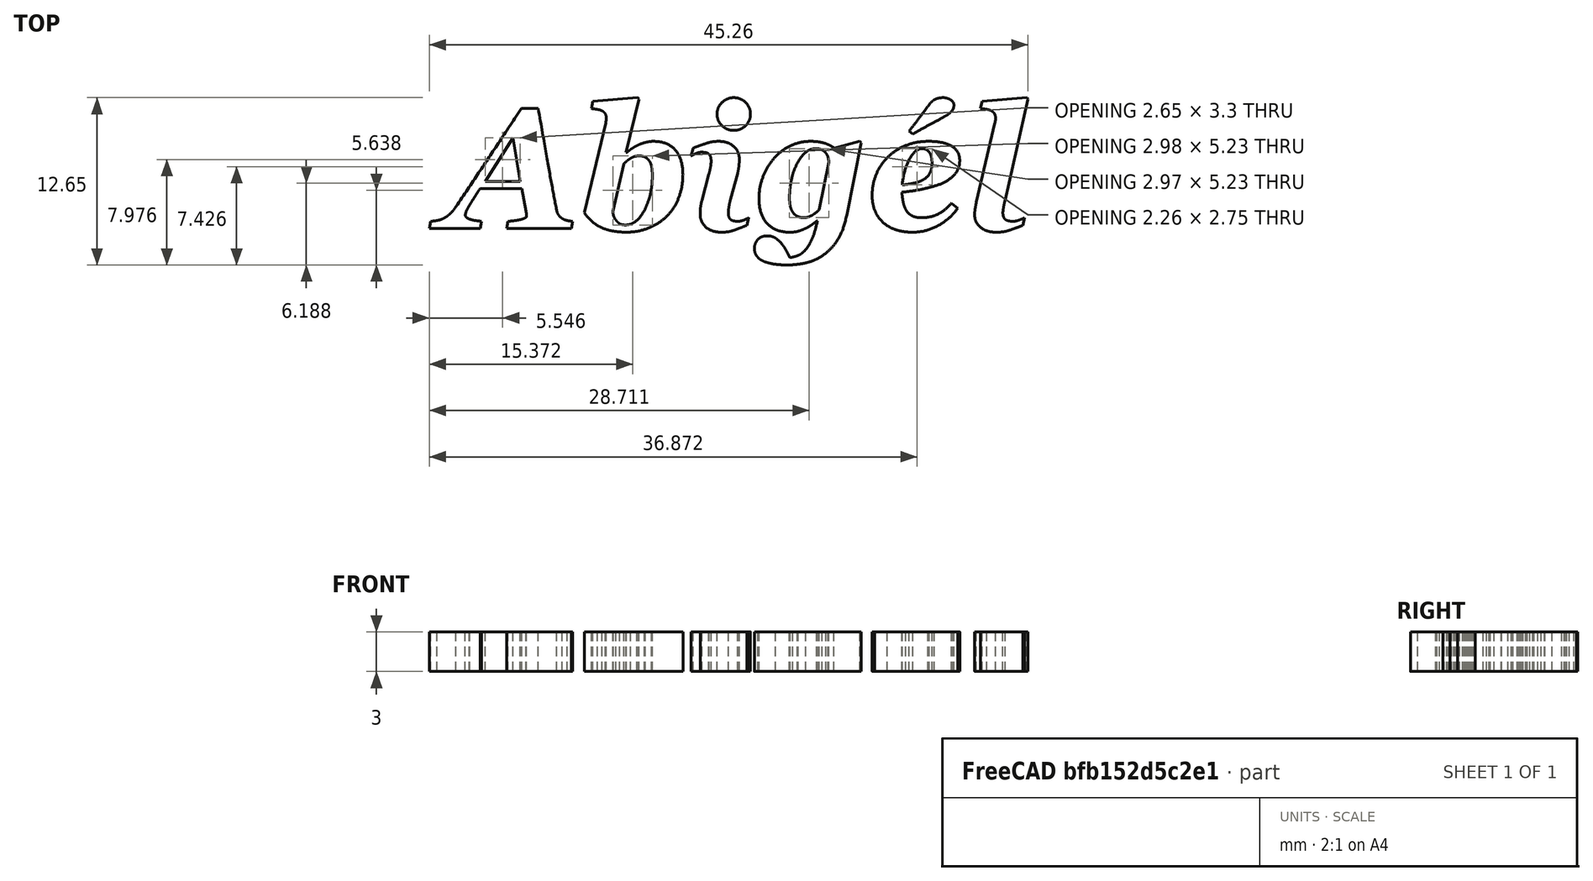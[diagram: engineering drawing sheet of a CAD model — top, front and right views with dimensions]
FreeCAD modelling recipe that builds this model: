
FCSTD DOCUMENT  (FreeCAD 0.17R13541 (Git))
Label: Aby
License: All rights reserved
LicenseURL: http://en.wikipedia.org/wiki/All_rights_reserved
objects: Sketcher::SketchObject×1, Part::Extrusion×1
note: 2 computed .brp shape members not serialized (recipe doc carries the construction recipe); baked Part::Feature solids carry a one-line shape summary decoded from their .brp

FEATURE [Sketcher::SketchObject] Sketch
  sketch-geometry (226):
    g0: LineSegment StartX=4.71852 StartY=0 StartZ=0 EndX=4.83025 EndY=0.550064 EndZ=0
    g1: LineSegment StartX=9.61324 StartY=0 StartZ=0 EndX=4.71852 EndY=0 EndZ=0
    g2: LineSegment StartX=9.72067 StartY=0.550064 StartZ=0 EndX=9.61324 EndY=0 EndZ=0
    g3: BSplineCurve PolesCount=3 KnotsCount=2 Degree=2 IsPeriodic=0
    g4: BSplineCurve PolesCount=3 KnotsCount=2 Degree=2 IsPeriodic=0
    g5: BSplineCurve PolesCount=3 KnotsCount=2 Degree=2 IsPeriodic=0
    g6: BSplineCurve PolesCount=3 KnotsCount=2 Degree=2 IsPeriodic=0
    g7: BSplineCurve PolesCount=3 KnotsCount=2 Degree=2 IsPeriodic=0
    g8: BSplineCurve PolesCount=3 KnotsCount=2 Degree=2 IsPeriodic=0
    g9: LineSegment StartX=5.83584 StartY=9.07606 StartZ=0 EndX=7.11216 EndY=9.07606 EndZ=0
    g10: BSplineCurve PolesCount=3 KnotsCount=2 Degree=2 IsPeriodic=0
    g11: BSplineCurve PolesCount=3 KnotsCount=2 Degree=2 IsPeriodic=0
    g12: BSplineCurve PolesCount=3 KnotsCount=2 Degree=2 IsPeriodic=0
    g13: BSplineCurve PolesCount=3 KnotsCount=2 Degree=2 IsPeriodic=0
    g14: BSplineCurve PolesCount=3 KnotsCount=2 Degree=2 IsPeriodic=0
    g15: BSplineCurve PolesCount=3 KnotsCount=2 Degree=2 IsPeriodic=0
    g16: LineSegment StartX=-1.12162 StartY=0 StartZ=0 EndX=-1.00988 EndY=0.550064 EndZ=0
    g17: LineSegment StartX=2.72024 StartY=0 StartZ=0 EndX=-1.12162 EndY=0 EndZ=0
    g18: LineSegment StartX=2.83197 StartY=0.550064 StartZ=0 EndX=2.72024 EndY=0 EndZ=0
    g19: BSplineCurve PolesCount=3 KnotsCount=2 Degree=2 IsPeriodic=0
    g20: BSplineCurve PolesCount=3 KnotsCount=2 Degree=2 IsPeriodic=0
    g21: BSplineCurve PolesCount=3 KnotsCount=2 Degree=2 IsPeriodic=0
    g22: BSplineCurve PolesCount=3 KnotsCount=2 Degree=2 IsPeriodic=0
    g23: BSplineCurve PolesCount=3 KnotsCount=2 Degree=2 IsPeriodic=0
    g24: BSplineCurve PolesCount=3 KnotsCount=2 Degree=2 IsPeriodic=0
    g25: LineSegment StartX=5.86592 StartY=3.02535 StartZ=0 EndX=2.71594 EndY=3.02535 EndZ=0
    g26: LineSegment StartX=6.18823 StartY=1.315 StartZ=0 EndX=5.86592 EndY=3.02535 EndZ=0
    g27: BSplineCurve PolesCount=3 KnotsCount=2 Degree=2 IsPeriodic=0
    g28: BSplineCurve PolesCount=3 KnotsCount=2 Degree=2 IsPeriodic=0
    g29: BSplineCurve PolesCount=3 KnotsCount=2 Degree=2 IsPeriodic=0
    g30: BSplineCurve PolesCount=3 KnotsCount=2 Degree=2 IsPeriodic=0
    g31: LineSegment StartX=5.74989 StartY=3.57542 StartZ=0 EndX=5.19123 EndY=6.87581 EndZ=0
    g32: LineSegment StartX=3.10271 StartY=3.57542 StartZ=0 EndX=5.74989 EndY=3.57542 EndZ=0
    g33: LineSegment StartX=5.19123 StartY=6.87581 StartZ=0 EndX=3.10271 EndY=3.57542 EndZ=0
    g34: BSplineCurve PolesCount=3 KnotsCount=2 Degree=2 IsPeriodic=0
    g35: BSplineCurve PolesCount=3 KnotsCount=2 Degree=2 IsPeriodic=0
    g36: BSplineCurve PolesCount=3 KnotsCount=2 Degree=2 IsPeriodic=0
    g37: BSplineCurve PolesCount=3 KnotsCount=2 Degree=2 IsPeriodic=0
    g38: BSplineCurve PolesCount=3 KnotsCount=2 Degree=2 IsPeriodic=0
    g39: BSplineCurve PolesCount=3 KnotsCount=2 Degree=2 IsPeriodic=0
    g40: BSplineCurve PolesCount=3 KnotsCount=2 Degree=2 IsPeriodic=0
    g41: LineSegment StartX=13.743 StartY=5.7413 StartZ=0 EndX=13.7903 EndY=5.7413 EndZ=0
    g42: LineSegment StartX=14.7185 StartY=9.80232 StartZ=0 EndX=13.743 EndY=5.7413 EndZ=0
    g43: LineSegment StartX=14.6498 StartY=9.90116 StartZ=0 EndX=14.7185 EndY=9.80232 EndZ=0
    g44: LineSegment StartX=11.2505 StartY=9.62613 StartZ=0 EndX=14.6498 EndY=9.90116 EndZ=0
    g45: LineSegment StartX=11.1345 StartY=9.07606 StartZ=0 EndX=11.2505 EndY=9.62613 EndZ=0
    g46: BSplineCurve PolesCount=3 KnotsCount=2 Degree=2 IsPeriodic=0
    g47: BSplineCurve PolesCount=3 KnotsCount=2 Degree=2 IsPeriodic=0
    g48: BSplineCurve PolesCount=3 KnotsCount=2 Degree=2 IsPeriodic=0
    g49: BSplineCurve PolesCount=3 KnotsCount=2 Degree=2 IsPeriodic=0
    g50: BSplineCurve PolesCount=3 KnotsCount=2 Degree=2 IsPeriodic=0
    g51: BSplineCurve PolesCount=3 KnotsCount=2 Degree=2 IsPeriodic=0
    g52: LineSegment StartX=10.593 StartY=1.21616 StartZ=0 EndX=12.2089 EndY=7.98023 EndZ=0
    g53: BSplineCurve PolesCount=3 KnotsCount=2 Degree=2 IsPeriodic=0
    g54: BSplineCurve PolesCount=3 KnotsCount=2 Degree=2 IsPeriodic=0
    g55: BSplineCurve PolesCount=3 KnotsCount=2 Degree=2 IsPeriodic=0
    g56: BSplineCurve PolesCount=3 KnotsCount=2 Degree=2 IsPeriodic=0
    g57: BSplineCurve PolesCount=3 KnotsCount=2 Degree=2 IsPeriodic=0
    g58: BSplineCurve PolesCount=3 KnotsCount=2 Degree=2 IsPeriodic=0
    g59: BSplineCurve PolesCount=3 KnotsCount=2 Degree=2 IsPeriodic=0
    g60: BSplineCurve PolesCount=3 KnotsCount=2 Degree=2 IsPeriodic=0
    g61: BSplineCurve PolesCount=3 KnotsCount=2 Degree=2 IsPeriodic=0
    g62: BSplineCurve PolesCount=3 KnotsCount=2 Degree=2 IsPeriodic=0
    g63: BSplineCurve PolesCount=3 KnotsCount=2 Degree=2 IsPeriodic=0
    g64: BSplineCurve PolesCount=3 KnotsCount=2 Degree=2 IsPeriodic=0
    g65: BSplineCurve PolesCount=3 KnotsCount=2 Degree=2 IsPeriodic=0
    g66: BSplineCurve PolesCount=3 KnotsCount=2 Degree=2 IsPeriodic=0
    g67: BSplineCurve PolesCount=3 KnotsCount=2 Degree=2 IsPeriodic=0
    g68: BSplineCurve PolesCount=3 KnotsCount=2 Degree=2 IsPeriodic=0
    g69: LineSegment StartX=13.5754 StartY=4.89042 StartZ=0 EndX=12.7632 EndY=1.29781 EndZ=0
    g70: BSplineCurve PolesCount=3 KnotsCount=2 Degree=2 IsPeriodic=0
    g71: BSplineCurve PolesCount=3 KnotsCount=2 Degree=2 IsPeriodic=0
    g72: BSplineCurve PolesCount=3 KnotsCount=2 Degree=2 IsPeriodic=0
    g73: BSplineCurve PolesCount=3 KnotsCount=2 Degree=2 IsPeriodic=0
    g74: BSplineCurve PolesCount=3 KnotsCount=2 Degree=2 IsPeriodic=0
    g75: LineSegment StartX=23.0254 StartY=0.825097 StartZ=0 EndX=22.8835 EndY=0.240653 EndZ=0
    g76: BSplineCurve PolesCount=3 KnotsCount=2 Degree=2 IsPeriodic=0
    g77: BSplineCurve PolesCount=3 KnotsCount=2 Degree=2 IsPeriodic=0
    g78: BSplineCurve PolesCount=3 KnotsCount=2 Degree=2 IsPeriodic=0
    g79: BSplineCurve PolesCount=3 KnotsCount=2 Degree=2 IsPeriodic=0
    g80: BSplineCurve PolesCount=3 KnotsCount=2 Degree=2 IsPeriodic=0
    g81: BSplineCurve PolesCount=3 KnotsCount=2 Degree=2 IsPeriodic=0
    g82: LineSegment StartX=22.1788 StartY=4.16846 StartZ=0 EndX=21.6502 EndY=2.21745 EndZ=0
    g83: BSplineCurve PolesCount=3 KnotsCount=2 Degree=2 IsPeriodic=0
    g84: BSplineCurve PolesCount=3 KnotsCount=2 Degree=2 IsPeriodic=0
    g85: BSplineCurve PolesCount=3 KnotsCount=2 Degree=2 IsPeriodic=0
    g86: BSplineCurve PolesCount=3 KnotsCount=2 Degree=2 IsPeriodic=0
    g87: BSplineCurve PolesCount=3 KnotsCount=2 Degree=2 IsPeriodic=0
    g88: BSplineCurve PolesCount=3 KnotsCount=2 Degree=2 IsPeriodic=0
    g89: LineSegment StartX=18.6721 StartY=5.50064 StartZ=0 EndX=18.8139 EndY=6.08509 EndZ=0
    g90: BSplineCurve PolesCount=3 KnotsCount=2 Degree=2 IsPeriodic=0
    g91: BSplineCurve PolesCount=3 KnotsCount=2 Degree=2 IsPeriodic=0
    g92: BSplineCurve PolesCount=3 KnotsCount=2 Degree=2 IsPeriodic=0
    g93: BSplineCurve PolesCount=3 KnotsCount=2 Degree=2 IsPeriodic=0
    g94: BSplineCurve PolesCount=3 KnotsCount=2 Degree=2 IsPeriodic=0
    g95: BSplineCurve PolesCount=3 KnotsCount=2 Degree=2 IsPeriodic=0
    g96: LineSegment StartX=19.4843 StartY=2.14869 StartZ=0 EndX=20.0129 EndY=4.10829 EndZ=0
    g97: BSplineCurve PolesCount=3 KnotsCount=2 Degree=2 IsPeriodic=0
    g98: BSplineCurve PolesCount=3 KnotsCount=2 Degree=2 IsPeriodic=0
    g99: BSplineCurve PolesCount=3 KnotsCount=2 Degree=2 IsPeriodic=0
    g100: BSplineCurve PolesCount=3 KnotsCount=2 Degree=2 IsPeriodic=0
    g101: BSplineCurve PolesCount=3 KnotsCount=2 Degree=2 IsPeriodic=0
    g102: BSplineCurve PolesCount=3 KnotsCount=2 Degree=2 IsPeriodic=0
    g103: BSplineCurve PolesCount=3 KnotsCount=2 Degree=2 IsPeriodic=0
    g104: BSplineCurve PolesCount=3 KnotsCount=2 Degree=2 IsPeriodic=0
    g105: BSplineCurve PolesCount=3 KnotsCount=2 Degree=2 IsPeriodic=0
    g106: BSplineCurve PolesCount=3 KnotsCount=2 Degree=2 IsPeriodic=0
    g107: BSplineCurve PolesCount=3 KnotsCount=2 Degree=2 IsPeriodic=0
    g108: BSplineCurve PolesCount=3 KnotsCount=2 Degree=2 IsPeriodic=0
    g109: BSplineCurve PolesCount=3 KnotsCount=2 Degree=2 IsPeriodic=0
    g110: BSplineCurve PolesCount=3 KnotsCount=2 Degree=2 IsPeriodic=0
    g111: LineSegment StartX=28.2123 StartY=0.571551 StartZ=0 EndX=28.1607 EndY=0.571551 EndZ=0
    g112: BSplineCurve PolesCount=3 KnotsCount=2 Degree=2 IsPeriodic=0
    g113: BSplineCurve PolesCount=3 KnotsCount=2 Degree=2 IsPeriodic=0
    g114: BSplineCurve PolesCount=3 KnotsCount=2 Degree=2 IsPeriodic=0
    g115: BSplineCurve PolesCount=3 KnotsCount=2 Degree=2 IsPeriodic=0
    g116: BSplineCurve PolesCount=3 KnotsCount=2 Degree=2 IsPeriodic=0
    g117: BSplineCurve PolesCount=3 KnotsCount=2 Degree=2 IsPeriodic=0
    g118: BSplineCurve PolesCount=3 KnotsCount=2 Degree=2 IsPeriodic=0
    g119: BSplineCurve PolesCount=3 KnotsCount=2 Degree=2 IsPeriodic=0
    g120: BSplineCurve PolesCount=3 KnotsCount=2 Degree=2 IsPeriodic=0
    g121: BSplineCurve PolesCount=3 KnotsCount=2 Degree=2 IsPeriodic=0
    g122: BSplineCurve PolesCount=3 KnotsCount=2 Degree=2 IsPeriodic=0
    g123: BSplineCurve PolesCount=3 KnotsCount=2 Degree=2 IsPeriodic=0
    g124: BSplineCurve PolesCount=3 KnotsCount=2 Degree=2 IsPeriodic=0
    g125: BSplineCurve PolesCount=3 KnotsCount=2 Degree=2 IsPeriodic=0
    g126: BSplineCurve PolesCount=3 KnotsCount=2 Degree=2 IsPeriodic=0
    g127: BSplineCurve PolesCount=3 KnotsCount=2 Degree=2 IsPeriodic=0
    g128: BSplineCurve PolesCount=3 KnotsCount=2 Degree=2 IsPeriodic=0
    g129: BSplineCurve PolesCount=3 KnotsCount=2 Degree=2 IsPeriodic=0
    g130: LineSegment StartX=31.5342 StartY=6.49334 StartZ=0 EndX=30.4383 EndY=1.02707 EndZ=0
    g131: LineSegment StartX=31.4439 StartY=6.60077 StartZ=0 EndX=31.5342 EndY=6.49334 EndZ=0
    g132: LineSegment StartX=29.4757 StartY=6.08509 StartZ=0 EndX=31.4439 EndY=6.60077 EndZ=0
    g133: BSplineCurve PolesCount=3 KnotsCount=2 Degree=2 IsPeriodic=0
    g134: BSplineCurve PolesCount=3 KnotsCount=2 Degree=2 IsPeriodic=0
    g135: BSplineCurve PolesCount=3 KnotsCount=2 Degree=2 IsPeriodic=0
    g136: BSplineCurve PolesCount=3 KnotsCount=2 Degree=2 IsPeriodic=0
    g137: BSplineCurve PolesCount=3 KnotsCount=2 Degree=2 IsPeriodic=0
    g138: BSplineCurve PolesCount=3 KnotsCount=2 Degree=2 IsPeriodic=0
    g139: BSplineCurve PolesCount=3 KnotsCount=2 Degree=2 IsPeriodic=0
    g140: BSplineCurve PolesCount=3 KnotsCount=2 Degree=2 IsPeriodic=0
    g141: BSplineCurve PolesCount=3 KnotsCount=2 Degree=2 IsPeriodic=0
    g142: BSplineCurve PolesCount=3 KnotsCount=2 Degree=2 IsPeriodic=0
    g143: BSplineCurve PolesCount=3 KnotsCount=2 Degree=2 IsPeriodic=0
    g144: BSplineCurve PolesCount=3 KnotsCount=2 Degree=2 IsPeriodic=0
    g145: BSplineCurve PolesCount=3 KnotsCount=2 Degree=2 IsPeriodic=0
    g146: LineSegment StartX=28.367 StartY=1.44822 StartZ=0 EndX=29.0761 EndY=5.01504 EndZ=0
    g147: BSplineCurve PolesCount=3 KnotsCount=2 Degree=2 IsPeriodic=0
    g148: BSplineCurve PolesCount=3 KnotsCount=2 Degree=2 IsPeriodic=0
    g149: BSplineCurve PolesCount=3 KnotsCount=2 Degree=2 IsPeriodic=0
    g150: BSplineCurve PolesCount=3 KnotsCount=2 Degree=2 IsPeriodic=0
    g151: BSplineCurve PolesCount=3 KnotsCount=2 Degree=2 IsPeriodic=0
    g152: BSplineCurve PolesCount=3 KnotsCount=2 Degree=2 IsPeriodic=0
    g153: BSplineCurve PolesCount=3 KnotsCount=2 Degree=2 IsPeriodic=0
    g154: BSplineCurve PolesCount=3 KnotsCount=2 Degree=2 IsPeriodic=0
    g155: BSplineCurve PolesCount=3 KnotsCount=2 Degree=2 IsPeriodic=0
    g156: BSplineCurve PolesCount=3 KnotsCount=2 Degree=2 IsPeriodic=0
    g157: BSplineCurve PolesCount=3 KnotsCount=2 Degree=2 IsPeriodic=0
    g158: BSplineCurve PolesCount=3 KnotsCount=2 Degree=2 IsPeriodic=0
    g159: BSplineCurve PolesCount=3 KnotsCount=2 Degree=2 IsPeriodic=0
    g160: BSplineCurve PolesCount=3 KnotsCount=2 Degree=2 IsPeriodic=0
    g161: BSplineCurve PolesCount=3 KnotsCount=2 Degree=2 IsPeriodic=0
    g162: BSplineCurve PolesCount=3 KnotsCount=2 Degree=2 IsPeriodic=0
    g163: LineSegment StartX=38.3455 StartY=1.92523 StartZ=0 EndX=38.8139 EndY=1.53416 EndZ=0
    g164: BSplineCurve PolesCount=3 KnotsCount=2 Degree=2 IsPeriodic=0
    g165: BSplineCurve PolesCount=3 KnotsCount=2 Degree=2 IsPeriodic=0
    g166: BSplineCurve PolesCount=3 KnotsCount=2 Degree=2 IsPeriodic=0
    g167: BSplineCurve PolesCount=3 KnotsCount=2 Degree=2 IsPeriodic=0
    g168: BSplineCurve PolesCount=3 KnotsCount=2 Degree=2 IsPeriodic=0
    g169: BSplineCurve PolesCount=3 KnotsCount=2 Degree=2 IsPeriodic=0
    g170: BSplineCurve PolesCount=3 KnotsCount=2 Degree=2 IsPeriodic=0
    g171: BSplineCurve PolesCount=3 KnotsCount=2 Degree=2 IsPeriodic=0
    g172: BSplineCurve PolesCount=3 KnotsCount=2 Degree=2 IsPeriodic=0
    g173: BSplineCurve PolesCount=3 KnotsCount=2 Degree=2 IsPeriodic=0
    g174: BSplineCurve PolesCount=3 KnotsCount=2 Degree=2 IsPeriodic=0
    g175: BSplineCurve PolesCount=3 KnotsCount=2 Degree=2 IsPeriodic=0
    g176: BSplineCurve PolesCount=3 KnotsCount=2 Degree=2 IsPeriodic=0
    g177: BSplineCurve PolesCount=3 KnotsCount=2 Degree=2 IsPeriodic=0
    g178: BSplineCurve PolesCount=3 KnotsCount=2 Degree=2 IsPeriodic=0
    g179: BSplineCurve PolesCount=3 KnotsCount=2 Degree=2 IsPeriodic=0
    g180: BSplineCurve PolesCount=3 KnotsCount=2 Degree=2 IsPeriodic=0
    g181: BSplineCurve PolesCount=3 KnotsCount=2 Degree=2 IsPeriodic=0
    g182: BSplineCurve PolesCount=3 KnotsCount=2 Degree=2 IsPeriodic=0
    g183: BSplineCurve PolesCount=3 KnotsCount=2 Degree=2 IsPeriodic=0
    g184: BSplineCurve PolesCount=3 KnotsCount=2 Degree=2 IsPeriodic=0
    g185: BSplineCurve PolesCount=3 KnotsCount=2 Degree=2 IsPeriodic=0
    g186: BSplineCurve PolesCount=3 KnotsCount=2 Degree=2 IsPeriodic=0
    g187: BSplineCurve PolesCount=3 KnotsCount=2 Degree=2 IsPeriodic=0
    g188: BSplineCurve PolesCount=3 KnotsCount=2 Degree=2 IsPeriodic=0
    g189: BSplineCurve PolesCount=3 KnotsCount=2 Degree=2 IsPeriodic=0
    g190: BSplineCurve PolesCount=3 KnotsCount=2 Degree=2 IsPeriodic=0
    g191: BSplineCurve PolesCount=3 KnotsCount=2 Degree=2 IsPeriodic=0
    g192: BSplineCurve PolesCount=3 KnotsCount=2 Degree=2 IsPeriodic=0
    g193: BSplineCurve PolesCount=3 KnotsCount=2 Degree=2 IsPeriodic=0
    g194: BSplineCurve PolesCount=3 KnotsCount=2 Degree=2 IsPeriodic=0
    g195: BSplineCurve PolesCount=3 KnotsCount=2 Degree=2 IsPeriodic=0
    g196: BSplineCurve PolesCount=3 KnotsCount=2 Degree=2 IsPeriodic=0
    g197: BSplineCurve PolesCount=3 KnotsCount=2 Degree=2 IsPeriodic=0
    g198: LineSegment StartX=35.4319 StartY=7.15084 StartZ=0 EndX=35.1612 EndY=7.3829 EndZ=0
    g199: BSplineCurve PolesCount=3 KnotsCount=2 Degree=2 IsPeriodic=0
    g200: BSplineCurve PolesCount=3 KnotsCount=2 Degree=2 IsPeriodic=0
    g201: BSplineCurve PolesCount=3 KnotsCount=2 Degree=2 IsPeriodic=0
    g202: LineSegment StartX=44.1384 StartY=9.79802 StartZ=0 EndX=42.4065 EndY=2.16588 EndZ=0
    g203: LineSegment StartX=44.0696 StartY=9.90116 StartZ=0 EndX=44.1384 EndY=9.79802 EndZ=0
    g204: LineSegment StartX=40.6704 StartY=9.62613 StartZ=0 EndX=44.0696 EndY=9.90116 EndZ=0
    g205: LineSegment StartX=40.5544 StartY=9.07606 StartZ=0 EndX=40.6704 EndY=9.62613 EndZ=0
    g206: BSplineCurve PolesCount=3 KnotsCount=2 Degree=2 IsPeriodic=0
    g207: BSplineCurve PolesCount=3 KnotsCount=2 Degree=2 IsPeriodic=0
    g208: BSplineCurve PolesCount=3 KnotsCount=2 Degree=2 IsPeriodic=0
    g209: BSplineCurve PolesCount=3 KnotsCount=2 Degree=2 IsPeriodic=0
    g210: BSplineCurve PolesCount=3 KnotsCount=2 Degree=2 IsPeriodic=0
    g211: BSplineCurve PolesCount=3 KnotsCount=2 Degree=2 IsPeriodic=0
    g212: LineSegment StartX=40.2407 StartY=2.01547 StartZ=0 EndX=41.633 EndY=7.96734 EndZ=0
    g213: BSplineCurve PolesCount=3 KnotsCount=2 Degree=2 IsPeriodic=0
    g214: BSplineCurve PolesCount=3 KnotsCount=2 Degree=2 IsPeriodic=0
    g215: BSplineCurve PolesCount=3 KnotsCount=2 Degree=2 IsPeriodic=0
    g216: BSplineCurve PolesCount=3 KnotsCount=2 Degree=2 IsPeriodic=0
    g217: BSplineCurve PolesCount=3 KnotsCount=2 Degree=2 IsPeriodic=0
    g218: BSplineCurve PolesCount=3 KnotsCount=2 Degree=2 IsPeriodic=0
    g219: LineSegment StartX=43.8762 StartY=0.825097 StartZ=0 EndX=43.7344 EndY=0.240653 EndZ=0
    g220: BSplineCurve PolesCount=3 KnotsCount=2 Degree=2 IsPeriodic=0
    g221: BSplineCurve PolesCount=3 KnotsCount=2 Degree=2 IsPeriodic=0
    g222: BSplineCurve PolesCount=3 KnotsCount=2 Degree=2 IsPeriodic=0
    g223: BSplineCurve PolesCount=3 KnotsCount=2 Degree=2 IsPeriodic=0
    g224: BSplineCurve PolesCount=3 KnotsCount=2 Degree=2 IsPeriodic=0
    g225: BSplineCurve PolesCount=3 KnotsCount=2 Degree=2 IsPeriodic=0
  constraints (233):
    c: Coincident(g0,g1)
    c: Horizontal(g1)
    c: Coincident(g1,g2)
    c: Coincident(g2,g3)
    c: Coincident(g3,g4)
    c: Coincident(g4,g5)
    c: Coincident(g5,g6)
    c: Coincident(g6,g7)
    c: Coincident(g7,g8)
    c: Coincident(g8,g9)
    c: Horizontal(g9)
    c: Coincident(g9,g10)
    c: Coincident(g10,g11)
    c: Coincident(g11,g12)
    c: Coincident(g12,g13)
    c: Coincident(g13,g14)
    c: Coincident(g14,g15)
    c: Coincident(g15,g16)
    c: Coincident(g16,g17)
    c: Horizontal(g17)
    c: Coincident(g17,g18)
    c: Coincident(g18,g19)
    c: Coincident(g19,g20)
    c: Coincident(g20,g21)
    c: Coincident(g21,g22)
    c: Coincident(g22,g23)
    c: Coincident(g23,g24)
    c: Coincident(g24,g25)
    c: Horizontal(g25)
    c: Coincident(g25,g26)
    c: Coincident(g26,g27)
    c: Coincident(g27,g28)
    c: Coincident(g28,g29)
    c: Coincident(g29,g30)
    c: Coincident(g30,g0)
    c: Coincident(g31,g32)
    c: Horizontal(g32)
    c: Coincident(g32,g33)
    c: Coincident(g33,g31)
    c: Coincident(g34,g35)
    c: Coincident(g35,g36)
    c: Coincident(g36,g37)
    c: Coincident(g37,g38)
    c: Coincident(g38,g39)
    c: Coincident(g39,g40)
    c: Coincident(g40,g41)
    c: Horizontal(g41)
    c: Coincident(g41,g42)
    c: Coincident(g42,g43)
    c: Coincident(g43,g44)
    c: Coincident(g44,g45)
    c: Coincident(g45,g46)
    c: Coincident(g46,g47)
    c: Coincident(g47,g48)
    c: Coincident(g48,g49)
    c: Coincident(g49,g50)
    c: Coincident(g50,g51)
    c: Coincident(g51,g52)
    c: Coincident(g52,g53)
    c: Coincident(g53,g54)
    c: Coincident(g54,g55)
    c: Coincident(g55,g56)
    c: Coincident(g56,g57)
    c: Coincident(g57,g58)
    c: Coincident(g58,g59)
    c: Coincident(g59,g34)
    c: Coincident(g60,g61)
    c: Coincident(g61,g62)
    c: Coincident(g62,g63)
    c: Coincident(g63,g64)
    c: Coincident(g64,g65)
    c: Coincident(g65,g66)
    c: Coincident(g66,g67)
    c: Coincident(g67,g68)
    c: Coincident(g68,g69)
    c: Coincident(g69,g70)
    c: Coincident(g70,g71)
    c: Coincident(g71,g72)
    c: Coincident(g72,g73)
    c: Coincident(g73,g74)
    c: Coincident(g74,g60)
    c: Coincident(g75,g76)
    c: Coincident(g76,g77)
    c: Coincident(g77,g78)
    c: Coincident(g78,g79)
    c: Coincident(g79,g80)
    c: Coincident(g80,g81)
    c: Coincident(g81,g82)
    c: Coincident(g82,g83)
    c: Coincident(g83,g84)
    c: Coincident(g84,g85)
    c: Coincident(g85,g86)
    c: Coincident(g86,g87)
    c: Coincident(g87,g88)
    c: Coincident(g88,g89)
    c: Coincident(g89,g90)
    c: Coincident(g90,g91)
    c: Coincident(g91,g92)
    c: Coincident(g92,g93)
    c: Coincident(g93,g94)
    c: Coincident(g94,g95)
    c: Coincident(g95,g96)
    c: Coincident(g96,g97)
    c: Coincident(g97,g98)
    c: Coincident(g98,g99)
    c: Coincident(g99,g100)
    c: Coincident(g100,g101)
    c: Coincident(g101,g102)
    c: Coincident(g102,g75)
    c: Coincident(g103,g104)
    c: Coincident(g104,g105)
    c: Coincident(g105,g106)
    c: Coincident(g106,g107)
    c: Coincident(g107,g108)
    c: Coincident(g108,g109)
    c: Coincident(g109,g110)
    c: Coincident(g110,g103)
    c: Horizontal(g111)
    c: Coincident(g111,g112)
    c: Coincident(g112,g113)
    c: Coincident(g113,g114)
    c: Coincident(g114,g115)
    c: Coincident(g115,g116)
    c: Coincident(g116,g117)
    c: Coincident(g117,g118)
    c: Coincident(g118,g119)
    c: Coincident(g119,g120)
    c: Coincident(g120,g121)
    c: Coincident(g121,g122)
    c: Coincident(g122,g123)
    c: Coincident(g123,g124)
    c: Coincident(g124,g125)
    c: Coincident(g125,g126)
    c: Coincident(g126,g127)
    c: Coincident(g127,g128)
    c: Coincident(g128,g129)
    c: Coincident(g129,g130)
    c: Coincident(g130,g131)
    c: Coincident(g131,g132)
    c: Coincident(g132,g133)
    c: Coincident(g133,g134)
    c: Coincident(g134,g135)
    c: Coincident(g135,g136)
    c: Coincident(g136,g137)
    c: Coincident(g137,g138)
    c: Coincident(g138,g139)
    c: Coincident(g139,g140)
    c: Coincident(g140,g141)
    c: Coincident(g141,g142)
    c: Coincident(g142,g143)
    c: Coincident(g143,g144)
    c: Coincident(g144,g111)
    c: Coincident(g145,g146)
    c: Coincident(g146,g147)
    c: Coincident(g147,g148)
    c: Coincident(g148,g149)
    c: Coincident(g149,g150)
    c: Coincident(g150,g151)
    c: Coincident(g151,g152)
    c: Coincident(g152,g153)
    c: Coincident(g153,g154)
    c: Coincident(g154,g155)
    c: Coincident(g155,g156)
    c: Coincident(g156,g157)
    c: Coincident(g157,g158)
    c: Coincident(g158,g159)
    c: Coincident(g159,g145)
    c: Coincident(g160,g161)
    c: Coincident(g161,g162)
    c: Coincident(g162,g163)
    c: Coincident(g163,g164)
    c: Coincident(g164,g165)
    c: Coincident(g165,g166)
    c: Coincident(g166,g167)
    c: Coincident(g167,g168)
    c: Coincident(g168,g169)
    c: Coincident(g169,g170)
    c: Coincident(g170,g171)
    c: Coincident(g171,g172)
    c: Coincident(g172,g173)
    c: Coincident(g173,g174)
    c: Coincident(g174,g175)
    c: Coincident(g175,g176)
    c: Coincident(g176,g177)
    c: Coincident(g177,g178)
    c: Coincident(g178,g179)
    c: Coincident(g179,g180)
    c: Coincident(g180,g181)
    c: Coincident(g181,g182)
    c: Coincident(g182,g160)
    c: Coincident(g183,g184)
    c: Coincident(g184,g185)
    c: Coincident(g185,g186)
    c: Coincident(g186,g187)
    c: Coincident(g187,g188)
    c: Coincident(g188,g189)
    c: Coincident(g189,g190)
    c: Coincident(g190,g183)
    c: Coincident(g191,g192)
    c: Coincident(g192,g193)
    c: Coincident(g193,g194)
    c: Coincident(g194,g195)
    c: Coincident(g195,g196)
    c: Coincident(g196,g197)
    c: Coincident(g197,g198)
    c: Coincident(g198,g199)
    c: Coincident(g199,g200)
    c: Coincident(g200,g201)
    c: Coincident(g201,g191)
    c: Coincident(g202,g203)
    c: Coincident(g203,g204)
    c: Coincident(g204,g205)
    c: Coincident(g205,g206)
    c: Coincident(g206,g207)
    c: Coincident(g207,g208)
    c: Coincident(g208,g209)
    c: Coincident(g209,g210)
    c: Coincident(g210,g211)
    c: Coincident(g211,g212)
    c: Coincident(g212,g213)
    c: Coincident(g213,g214)
    c: Coincident(g214,g215)
    c: Coincident(g215,g216)
    c: Coincident(g216,g217)
    c: Coincident(g217,g218)
    c: Coincident(g218,g219)
    c: Coincident(g219,g220)
    c: Coincident(g220,g221)
    c: Coincident(g221,g222)
    c: Coincident(g222,g223)
    c: Coincident(g223,g224)
    c: Coincident(g224,g225)
    c: Coincident(g225,g202)
FEATURE [Part::Extrusion] Extrude
  Base = -> Sketch
  Dir = (0,0,1)
  DirMode = 2
  FaceMakerClass = Part::FaceMakerBullseye
  LengthFwd = 3
  LengthRev = 0
  Solid = true
  Symmetric = false
